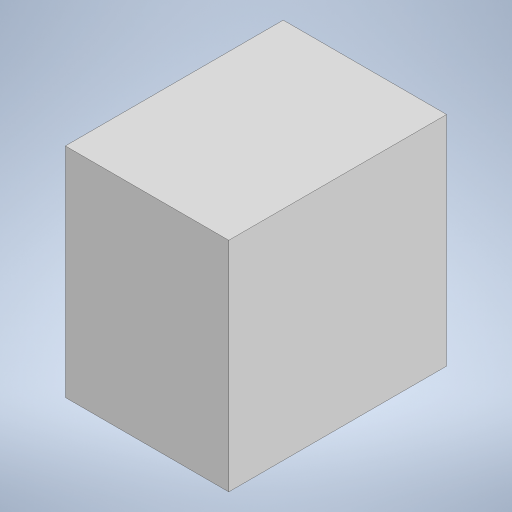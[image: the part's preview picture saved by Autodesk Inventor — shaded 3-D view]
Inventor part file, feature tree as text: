
AUTODESK INVENTOR PART (.ipt)
format: ipt  version: 2023 (Build 270158000, 158)  size: 162,304 bytes
history: native  units: mm
features: extrude x1, sketch x1
ambient origin geometry x8: Origin, YZ Plane, XZ Plane, XY Plane, X Axis, Y Axis, Z Axis, Center Point
bodies: Solid1 (feature_tree)
feature tree (2):
  extrude  "Extrusion1"  Depth=20.0mm
  sketch  "Sketch1"  dims[d0=15.0mm d1=20.0mm d2=20.0mm d3=0.0mm]
